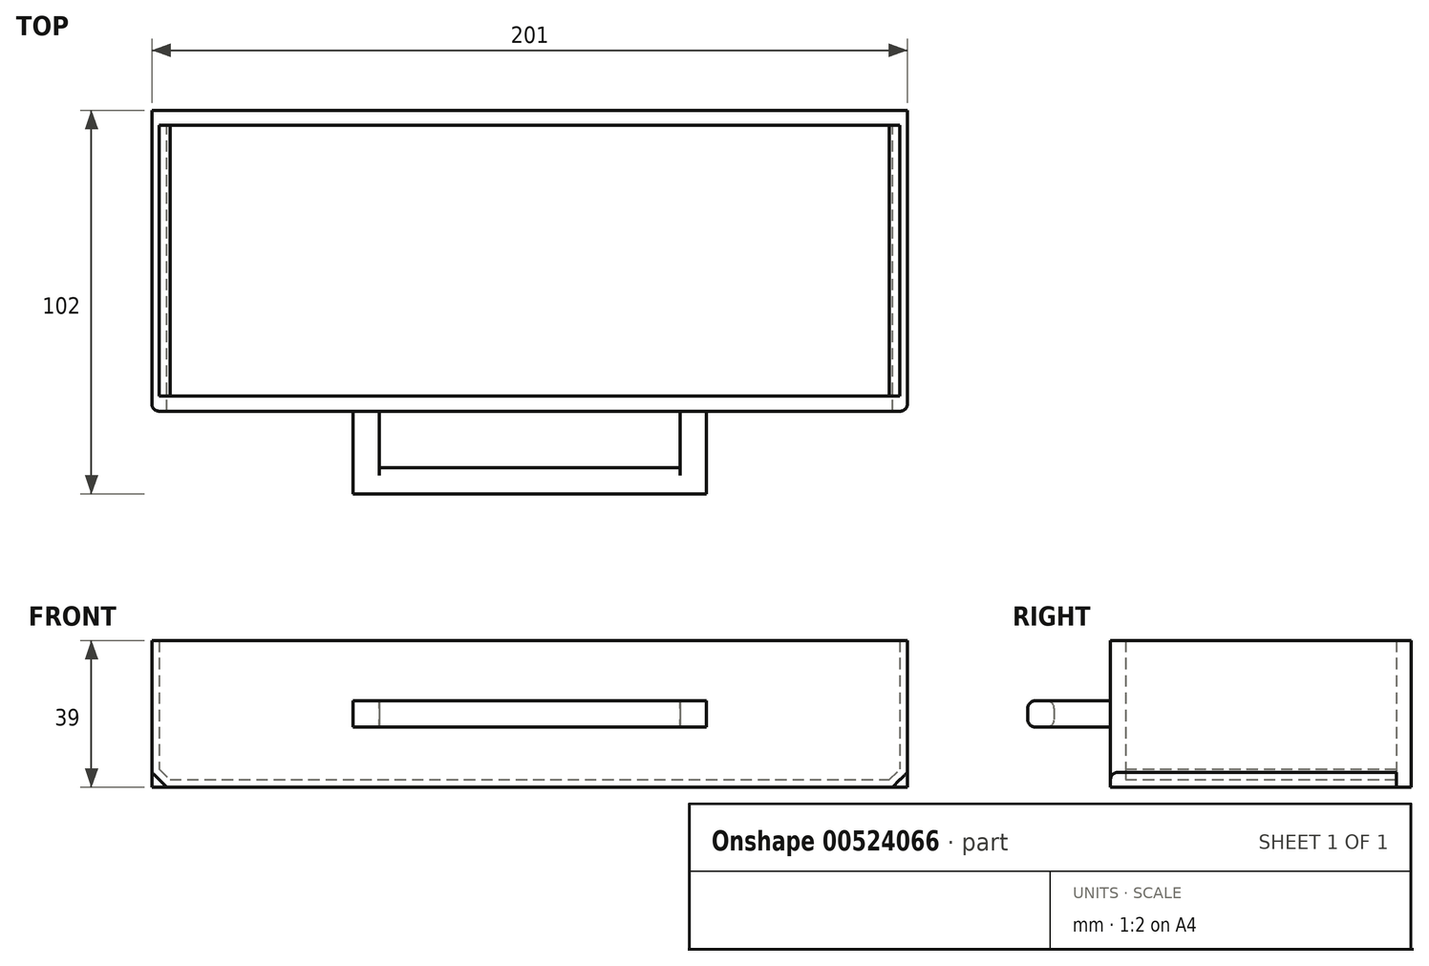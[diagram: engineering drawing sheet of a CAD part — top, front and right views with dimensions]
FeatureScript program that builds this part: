
annotation { "Feature Type Name" : "Feature", "Feature Type Description" : "" }
export const myFeature = defineFeature(function(context is Context, id is Id, definition is map)
    precondition{}
    {
        {
            var Q0;
            Q0=qCreatedBy(makeId("Front.planeOp"),FACE);
            var sketch = newSketch(context, id + "F0", { "sketchPlane" : qUnion([Q0])});
            skLineSegment(sketch, "E0.bottom", {"start": v(-94.88, 18.02) * mm, "end": v(-92.88, 18.02) * mm});
            skLineSegment(sketch, "E0.left", {"start": v(-94.88, 18.02) * mm, "end": v(-94.88, -16.97) * mm});
            skLineSegment(sketch, "E0.right", {"start": v(106.12, 18.02) * mm, "end": v(106.12, -16.97) * mm});
            skLineSegment(sketch, "E1.bottom", {"start": v(106.12, 18.02) * mm, "end": v(104.12, 18.02) * mm});
            skLineSegment(sketch, "E1.right", {"start": v(104.12, 18.02) * mm, "end": v(104.12, -16.15) * mm});
            skLineSegment(sketch, "E2.right", {"start": v(-92.88, 18.02) * mm, "end": v(-92.88, -16.15) * mm});
            skLineSegment(sketch, "E3.trimOffspring", {"start": v(104.12, 18.02) * mm, "end": v(106.12, 18.02) * mm});
            skLineSegment(sketch, "E4.trimOffspring", {"start": v(-90.04, -18.98) * mm, "end": v(101.3, -18.98) * mm});
            skLineSegment(sketch, "E5.trimOffspring", {"start": v(-90.87, -20.98) * mm, "end": v(102.12, -20.98) * mm});
            skLineSegment(sketch, "E6", {"start": v(101.3, -18.98) * mm, "end": v(104.12, -16.15) * mm});
            skLineSegment(sketch, "E7", {"start": v(-94.88, -16.97) * mm, "end": v(-90.87, -20.98) * mm});
            skLineSegment(sketch, "E8", {"start": v(-92.88, -16.15) * mm, "end": v(-90.04, -18.98) * mm});
            skLineSegment(sketch, "E9", {"start": v(106.12, -16.97) * mm, "end": v(102.12, -20.98) * mm});
            skSolve(sketch);
        }
        {
            var Q0;
            Q0 = qSketchRegion(id + "F0", true);
            extrude(context, id + "F1", {"entities" : qUnion([Q0]), "depth" : 72 * mm, "offsetDistance" : 25 * mm});
        }
        {
            var Q0;
            Q0=makeQuery(id+"F1.opExtrude","CAP_FACE",FACE,{"disambiguationData":[OSD([sQuery(id+"F0.wireOp",EDGE,"zQqWJa7y-pUKJ-xy1G-gMta-RPznTCvEpZ1M"),sQuery(id+"F0.wireOp",EDGE,"a9IDulpL-Ijgv-CQKY-ZfSg-mVPyYsMpTD7R.top"),sQuery(id+"F0.wireOp",EDGE,"EAkJThxj-IE8S-jt4G-SuQz-xiQeQ7hBqUW2"),sQuery(id+"F0.wireOp",EDGE,"E1.left"),sQuery(id+"F0.wireOp",EDGE,"E1.right"),sQuery(id+"F0.wireOp",EDGE,"E0.bottom"),sQuery(id+"F0.wireOp",EDGE,"E2.left"),sQuery(id+"F0.wireOp",EDGE,"E2.right"),sQuery(id+"F0.wireOp",EDGE,"Vc6FalZb-wMma-Ss9U-kOHa-5kO0ZZd0rlQQ"),sQuery(id+"F0.wireOp",EDGE,"0Gzg2qnO-fb3M-jGWa-QIIV-tmSLb963981d"),sQuery(id+"F0.wireOp",EDGE,"E3.trimOffspring"),sQuery(id+"F0.wireOp",EDGE,"0edb2488-ec7a-4db4-a124-8f56469d0e38.trimOffspring"),sQuery(id+"F0.wireOp",EDGE,"946b7aaa-86c3-4408-8b50-f4610018d49b.trimOffspring"),sQuery(id+"F0.wireOp",EDGE,"b67a2e25-b767-4d56-8d15-dcb9f4b7eb1d.trimOffspring"),sQuery(id+"F0.wireOp",EDGE,"E4.trimOffspring"),sQuery(id+"F0.wireOp",EDGE,"E5.trimOffspring")])],"isStart":true});
            var sketch = newSketch(context, id + "F2", { "sketchPlane" : qUnion([Q0])});
            skLineSegment(sketch, "E10.bottom", {"start": v(-106.12, 18.02) * mm, "end": v(94.88, 18.02) * mm});
            skLineSegment(sketch, "E10.top", {"start": v(-106.12, -20.98) * mm, "end": v(94.88, -20.98) * mm});
            skLineSegment(sketch, "E10.left", {"start": v(-106.12, 18.02) * mm, "end": v(-106.12, -20.98) * mm});
            skLineSegment(sketch, "E10.right", {"start": v(94.88, 18.02) * mm, "end": v(94.88, -20.98) * mm});
            skSolve(sketch);
        }
        {
            var Q0;
            Q0 = qSketchRegion(id + "F2", true);
            extrude(context, id + "F3", {"entities" : qUnion([Q0]), "operationType" : NewBodyOperationType.ADD, "depth" : 4 * mm, "offsetDistance" : 25 * mm});
        }
        {
            var Q0;
            Q0=makeQuery(id+"F1.opExtrude","CAP_FACE",FACE,{"disambiguationData":[OSD([sQuery(id+"F0.wireOp",EDGE,"E1.left"),sQuery(id+"F0.wireOp",EDGE,"E1.right"),sQuery(id+"F0.wireOp",EDGE,"E0.bottom"),sQuery(id+"F0.wireOp",EDGE,"E2.left"),sQuery(id+"F0.wireOp",EDGE,"E2.right"),sQuery(id+"F0.wireOp",EDGE,"E3.trimOffspring"),sQuery(id+"F0.wireOp",EDGE,"E4.trimOffspring"),sQuery(id+"F0.wireOp",EDGE,"E5.trimOffspring"),sQuery(id+"F0.wireOp",EDGE,"E6"),sQuery(id+"F0.wireOp",EDGE,"E7"),sQuery(id+"F0.wireOp",EDGE,"E8"),sQuery(id+"F0.wireOp",EDGE,"E9")])],"isStart":false});
            var sketch = newSketch(context, id + "F4", { "sketchPlane" : qUnion([Q0])});
            skLineSegment(sketch, "E11", {"start": v(-94.88, 18.02) * mm, "end": v(-94.88, -16.97) * mm});
            skLineSegment(sketch, "E12", {"start": v(-94.88, -16.97) * mm, "end": v(-90.87, -20.98) * mm});
            skLineSegment(sketch, "E13", {"start": v(-90.87, -20.98) * mm, "end": v(102.12, -20.98) * mm});
            skLineSegment(sketch, "E14", {"start": v(102.12, -20.98) * mm, "end": v(106.12, -16.97) * mm});
            skLineSegment(sketch, "E15", {"start": v(106.12, -16.97) * mm, "end": v(106.12, 18.02) * mm});
            skLineSegment(sketch, "E16", {"start": v(-94.88, 18.02) * mm, "end": v(106.12, 18.02) * mm});
            skSolve(sketch);
        }
        {
            var Q0;
            Q0 = qSketchRegion(id + "F4", true);
            extrude(context, id + "F5", {"entities" : qUnion([Q0]), "operationType" : NewBodyOperationType.ADD, "depth" : 4 * mm, "offsetDistance" : 25 * mm});
        }
        {
            var Q0;
            Q0=makeQuery(id+"F5.opExtrude","CAP_EDGE",EDGE,{"disambiguationData":[OSD([sQuery(id+"F4.wireOp",EDGE,"E11")])],"isStart":false});
            var Q1;
            Q1=makeQuery(id+"F5.opExtrude","CAP_EDGE",EDGE,{"disambiguationData":[OSD([sQuery(id+"F4.wireOp",EDGE,"E15")])],"isStart":false});
            fillet(context, id + "F6", {"entities" : qUnion([Q0, Q1]), "radius" : 2 * mm, "tangentPropagation" : true, "allowEdgeOverflow" : false});
        }
        {
            var Q0;
            Q0=makeQuery(id+"F5.opExtrude","CAP_FACE",FACE,{"disambiguationData":[OSD([sQuery(id+"F4.wireOp",EDGE,"E11"),sQuery(id+"F4.wireOp",EDGE,"E12"),sQuery(id+"F4.wireOp",EDGE,"E13"),sQuery(id+"F4.wireOp",EDGE,"E14"),sQuery(id+"F4.wireOp",EDGE,"E15"),sQuery(id+"F4.wireOp",EDGE,"E16")])],"isStart":false});
            var sketch = newSketch(context, id + "F7", { "sketchPlane" : qUnion([Q0])});
            skLineSegment(sketch, "E17", {"start": v(-79.29, -1.48) * mm, "end": v(165.82, -1.48) * mm, "construction": true});
            skLineSegment(sketch, "E18", {"start": v(5.62, 42.87) * mm, "end": v(5.62, -42.27) * mm, "construction": true});
            skLineSegment(sketch, "E19", {"start": v(-79.3, 2.02) * mm, "end": v(118.51, 2.02) * mm, "construction": true});
            skLineSegment(sketch, "E20.bottom", {"start": v(-41.38, 2.02) * mm, "end": v(-34.38, 2.02) * mm});
            skLineSegment(sketch, "E20.top", {"start": v(-41.38, -4.98) * mm, "end": v(-34.38, -4.98) * mm});
            skLineSegment(sketch, "E20.left", {"start": v(-41.38, 2.02) * mm, "end": v(-41.38, -4.98) * mm});
            skLineSegment(sketch, "E20.right", {"start": v(-34.38, 2.02) * mm, "end": v(-34.38, -4.98) * mm});
            skLineSegment(sketch, "E21.MirrorCS", {"start": v(45.62, 2.02) * mm, "end": v(45.62, -4.98) * mm});
            skLineSegment(sketch, "E22.MirrorCS", {"start": v(52.62, 2.02) * mm, "end": v(52.62, -4.98) * mm});
            skLineSegment(sketch, "E23.MirrorCS", {"start": v(52.62, -4.98) * mm, "end": v(45.62, -4.98) * mm});
            skLineSegment(sketch, "E24", {"start": v(45.62, 2.02) * mm, "end": v(52.62, 2.02) * mm});
            skSolve(sketch);
        }
        {
            var Q0;
            Q0=makeQuery(id+"F7.imprint","IMPRINT",FACE,{"disambiguationData":[TD([[makeQuery(id+"F7.imprint","IMPRINT",EDGE,{"derivedFrom":sQuery(id+"F7.wireOp",EDGE,"E21.MirrorCS")}),1.0]])]});
            var Q1;
            Q1=makeQuery(id+"F7.imprint","IMPRINT",FACE,{"disambiguationData":[TD([[makeQuery(id+"F7.imprint","IMPRINT",EDGE,{"derivedFrom":sQuery(id+"F7.wireOp",EDGE,"E20.bottom")}),-1.0]])]});
            extrude(context, id + "F8", {"entities" : qUnion([Q0, Q1]), "operationType" : NewBodyOperationType.ADD, "depth" : 22 * mm, "offsetDistance" : 25 * mm});
        }
        {
            var Q0;
            Q0=makeQuery(id+"F8.opExtrude","SWEPT_FACE",FACE,{"disambiguationData":[OSD([sQuery(id+"F7.wireOp",EDGE,"E20.right")])]});
            var sketch = newSketch(context, id + "F9", { "sketchPlane" : qUnion([Q0])});
            skLineSegment(sketch, "E25.bottom", {"start": v(-98, 2.02) * mm, "end": v(-91, 2.02) * mm});
            skLineSegment(sketch, "E25.top", {"start": v(-98, -4.98) * mm, "end": v(-91, -4.98) * mm});
            skLineSegment(sketch, "E25.left", {"start": v(-98, 2.02) * mm, "end": v(-98, -4.98) * mm});
            skLineSegment(sketch, "E25.right", {"start": v(-91, 2.02) * mm, "end": v(-91, -4.98) * mm});
            skSolve(sketch);
        }
        {
            var Q0;
            Q0 = qSketchRegion(id + "F9", true);
            extrude(context, id + "F10", {"entities" : qUnion([Q0]), "operationType" : NewBodyOperationType.ADD, "depth" : 80 * mm, "offsetDistance" : 25 * mm});
        }
        {
            var Q0;
            Q0=makeQuery(id+"F10.boolean.opBoolean","MERGE",EDGE,{"derivedFrom":[makeQuery(id+"F8.opExtrude","CAP_EDGE",EDGE,{"disambiguationData":[OSD([sQuery(id+"F7.wireOp",EDGE,"E20.bottom")])],"isStart":false}),makeQuery(id+"F8.opExtrude","CAP_EDGE",EDGE,{"disambiguationData":[OSD([sQuery(id+"F7.wireOp",EDGE,"E24")])],"isStart":false}),makeQuery(id+"F10.opExtrude","SWEPT_EDGE",EDGE,{"disambiguationData":[OSD([sQuery(id+"F9.wireOp",EDGE,"E25.bottom"),sQuery(id+"F9.wireOp",EDGE,"E25.left")])]})]});
            var Q1;
            Q1=makeQuery(id+"F10.boolean.opBoolean","MERGE",EDGE,{"derivedFrom":[makeQuery(id+"F8.opExtrude","CAP_EDGE",EDGE,{"disambiguationData":[OSD([sQuery(id+"F7.wireOp",EDGE,"E20.top")])],"isStart":false}),makeQuery(id+"F8.opExtrude","CAP_EDGE",EDGE,{"disambiguationData":[OSD([sQuery(id+"F7.wireOp",EDGE,"E23.MirrorCS")])],"isStart":false}),makeQuery(id+"F10.opExtrude","SWEPT_EDGE",EDGE,{"disambiguationData":[OSD([sQuery(id+"F9.wireOp",EDGE,"E25.top"),sQuery(id+"F9.wireOp",EDGE,"E25.left")])]})]});
            var Q2;
            Q2=makeQuery(id+"F10.opExtrude","SWEPT_EDGE",EDGE,{"disambiguationData":[OSD([sQuery(id+"F7.wireOp",EDGE,"E20.bottom"),sQuery(id+"F7.wireOp",EDGE,"E20.right"),sQuery(id+"F9.wireOp",EDGE,"E25.bottom"),sQuery(id+"F9.wireOp",EDGE,"E25.right")])]});
            var Q3;
            Q3=makeQuery(id+"F10.opExtrude","SWEPT_EDGE",EDGE,{"disambiguationData":[OSD([sQuery(id+"F7.wireOp",EDGE,"E20.top"),sQuery(id+"F7.wireOp",EDGE,"E20.right"),sQuery(id+"F9.wireOp",EDGE,"E25.top"),sQuery(id+"F9.wireOp",EDGE,"E25.right")])]});
            fillet(context, id + "F11", {"entities" : qUnion([Q0, Q1, Q2, Q3]), "radius" : 2 * mm, "tangentPropagation" : true, "allowEdgeOverflow" : false});
        }
    });
